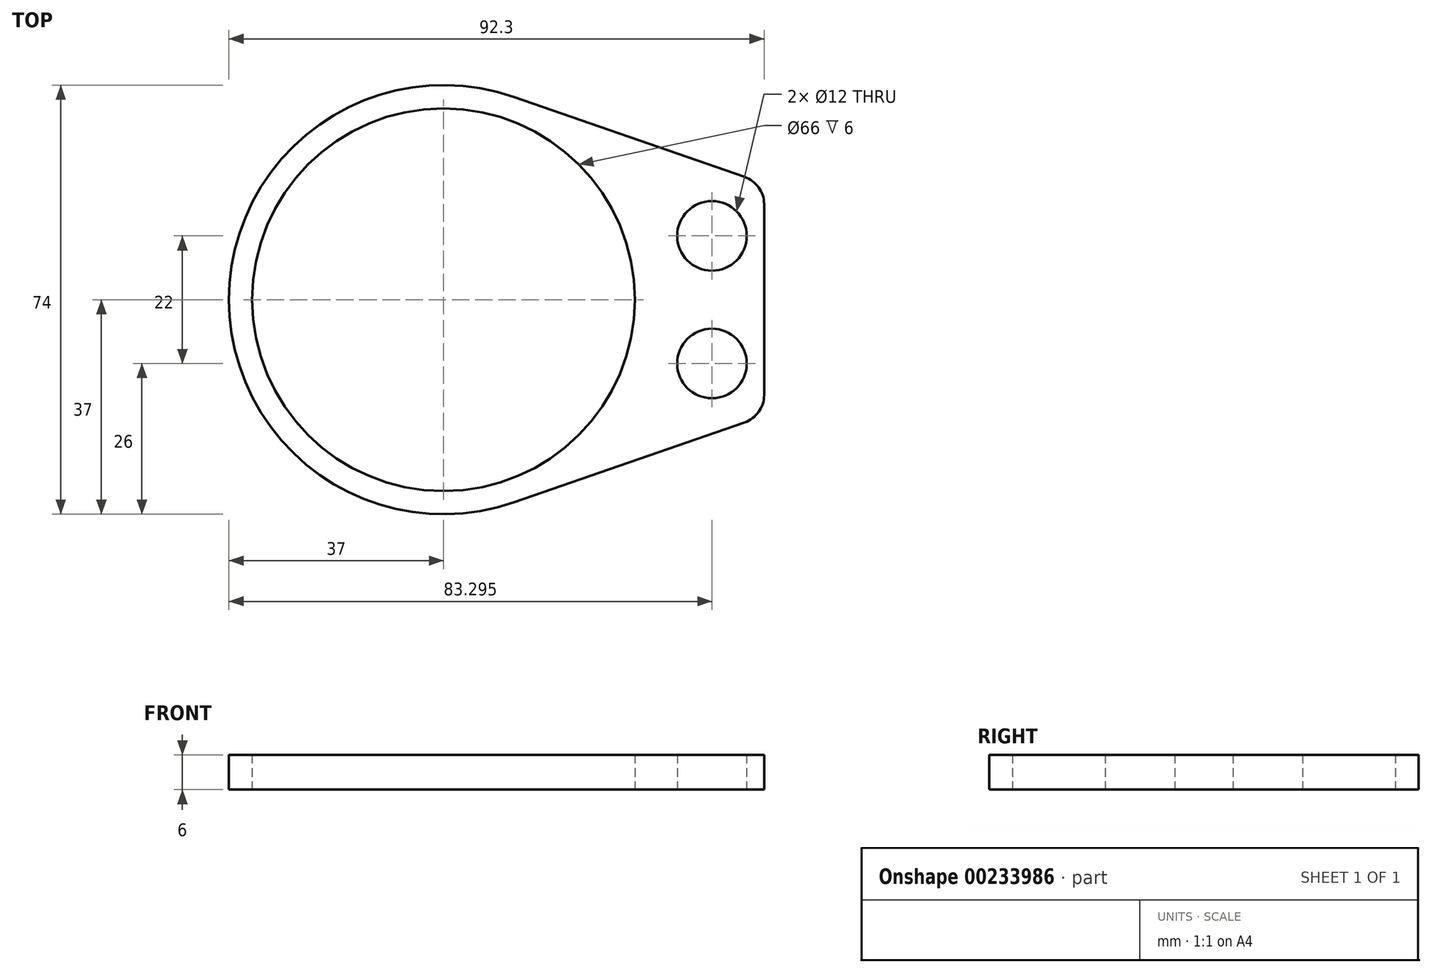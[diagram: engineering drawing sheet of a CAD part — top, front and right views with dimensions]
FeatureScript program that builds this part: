
annotation { "Feature Type Name" : "Feature", "Feature Type Description" : "" }
export const myFeature = defineFeature(function(context is Context, id is Id, definition is map)
    precondition{}
    {
        {
            var Q0;
            Q0=qCreatedBy(makeId("Top.planeOp"),FACE);
            var sketch = newSketch(context, id + "F0", { "sketchPlane" : qUnion([Q0])});
            skCircle(sketch, "E0", {"center": v(0, 0) * mm, "radius": 33 * mm});
            skCircle(sketch, "E1", {"center": v(46.3, 11) * mm, "radius": 6 * mm});
            skCircle(sketch, "E2", {"center": v(46.3, -11) * mm, "radius": 6 * mm});
            skCircle(sketch, "E3", {"center": v(0, 0) * mm, "radius": 37 * mm});
            skLineSegment(sketch, "E4", {"start": v(55.3, 16.44) * mm, "end": v(55.3, -16.44) * mm});
            skLineSegment(sketch, "E5", {"start": v(51.93, 21.17) * mm, "end": v(12.11, 34.96) * mm});
            skPoint(sketch, "E6.visualSharp", {"position": v(55.3, 20) * mm});
            skArc(sketch, "E6.filletArc", {"start": v(55.3, 16.44) * mm, "mid": v(54.37, 19.34) * mm, "end": v(51.93, 21.17) * mm});
            skLineSegment(sketch, "E7", {"start": v(51.93, -21.17) * mm, "end": v(12.11, -34.96) * mm});
            skPoint(sketch, "E8.visualSharp", {"position": v(55.3, -20) * mm});
            skArc(sketch, "E8.filletArc", {"start": v(51.93, -21.17) * mm, "mid": v(54.37, -19.34) * mm, "end": v(55.3, -16.44) * mm});
            skSolve(sketch);
        }
        {
            var Q0;
            Q0=makeQuery(id+"F0.imprint","IMPRINT",FACE,{"disambiguationData":[TD([[makeQuery(id+"F0.imprint","IMPRINT",EDGE,{"derivedFrom":sQuery(id+"F0.wireOp",EDGE,"E0")}),-1.0]])]});
            var Q1;
            Q1=makeQuery(id+"F0.imprint","IMPRINT",FACE,{"disambiguationData":[TD([[makeQuery(id+"F0.imprint","IMPRINT",EDGE,{"derivedFrom":sQuery(id+"F0.wireOp",EDGE,"E1")}),-1.0]])]});
            extrude(context, id + "F1", {"entities" : qUnion([Q0, Q1]), "depth" : 6 * mm});
        }
    });
